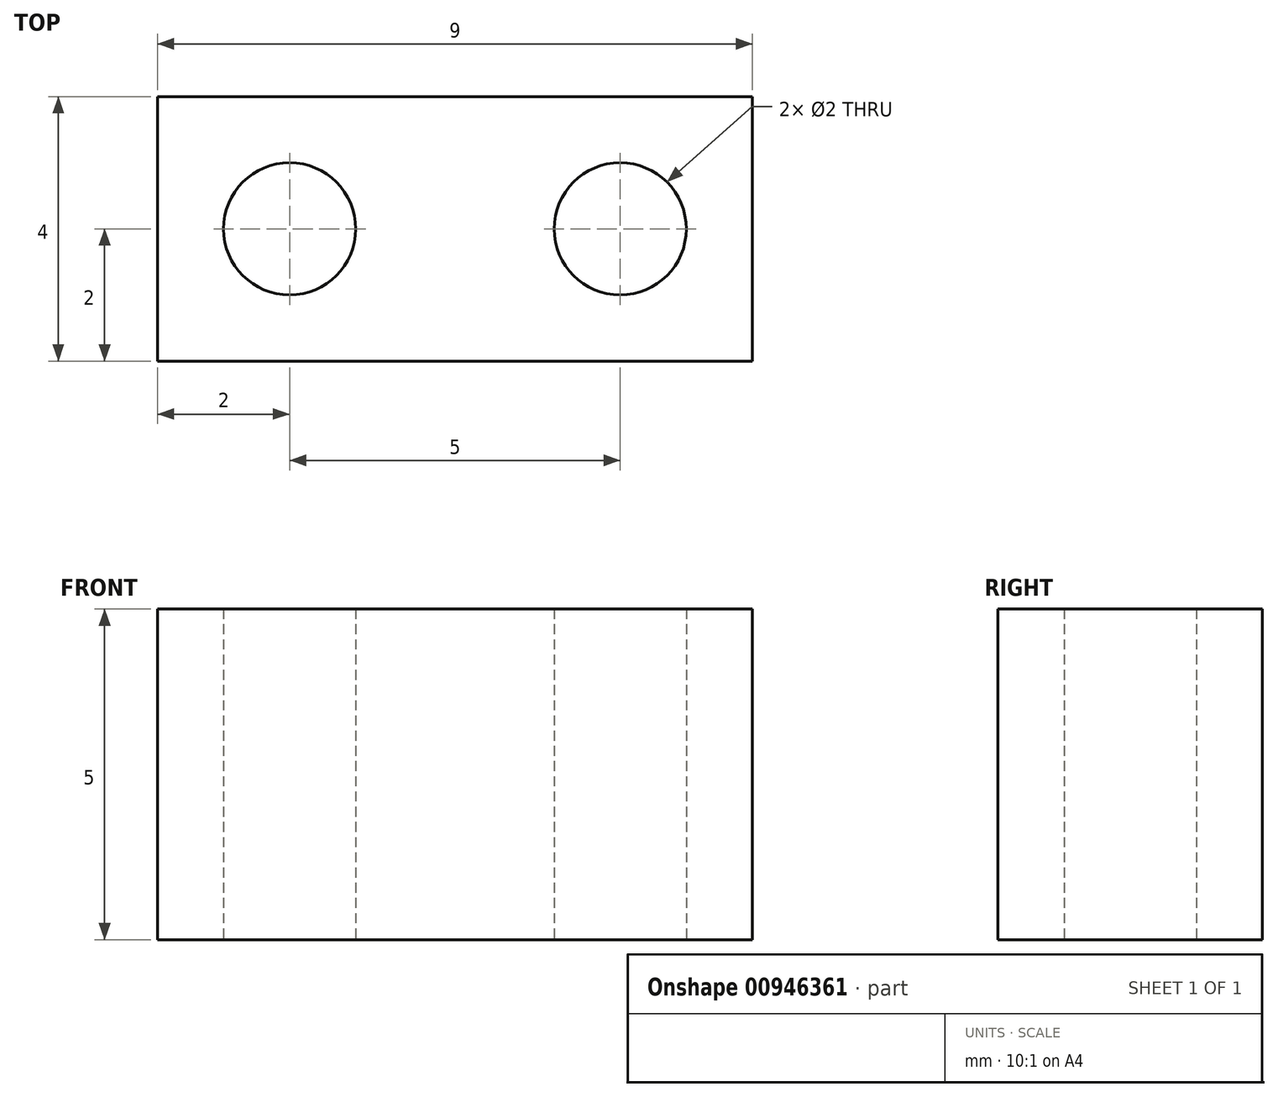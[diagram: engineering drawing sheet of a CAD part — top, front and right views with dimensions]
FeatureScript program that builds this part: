
annotation { "Feature Type Name" : "Feature", "Feature Type Description" : "" }
export const myFeature = defineFeature(function(context is Context, id is Id, definition is map)
    precondition{}
    {
        {
            var Q0;
            Q0=qCreatedBy(makeId("Top.planeOp"),FACE);
            var sketch = newSketch(context, id + "F0", { "sketchPlane" : qUnion([Q0])});
            skLineSegment(sketch, "E0.bottom", {"start": v(4.5, -2) * mm, "end": v(-4.5, -2) * mm});
            skLineSegment(sketch, "E0.top", {"start": v(4.5, 2) * mm, "end": v(-4.5, 2) * mm});
            skLineSegment(sketch, "E0.left", {"start": v(4.5, -2) * mm, "end": v(4.5, 2) * mm});
            skLineSegment(sketch, "E0.right", {"start": v(-4.5, -2) * mm, "end": v(-4.5, 2) * mm});
            skPoint(sketch, "E0.middle", {"position": v(0, 0) * mm});
            skLineSegment(sketch, "E1", {"start": v(0, 0) * mm, "end": v(-2.5, 0) * mm, "construction": true});
            skCircle(sketch, "E2", {"center": v(-2.5, 0) * mm, "radius": 1 * mm});
            skCircle(sketch, "E3.MirrorC", {"center": v(2.5, 0) * mm, "radius": 1 * mm});
            skSolve(sketch);
        }
        {
            var Q0;
            Q0=makeQuery(id+"F0.imprint","IMPRINT",FACE,{"disambiguationData":[TD([[makeQuery(id+"F0.imprint","IMPRINT",EDGE,{"derivedFrom":sQuery(id+"F0.wireOp",EDGE,"E0.bottom")}),-1.0]])]});
            extrude(context, id + "F1", {"entities" : qUnion([Q0]), "depth" : 5 * mm, "offsetDistance" : 25 * mm});
        }
        {
            var Q0;
            Q0=sQuery(id+"F0.wireOp",EDGE,"E2");
            var Q1;
            Q1=sQuery(id+"F0.wireOp",EDGE,"E3.MirrorC");
            extrude(context, id + "F2", {"bodyType" : ToolBodyType.SURFACE, "surfaceEntities" : qUnion([Q0, Q1]), "depth" : 10 * mm, "offsetDistance" : 25 * mm});
        }
    });
